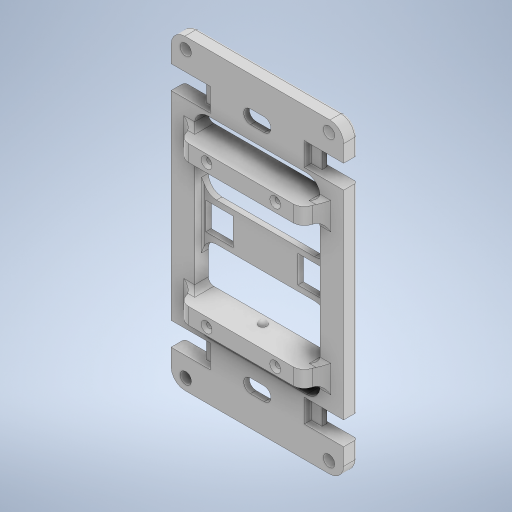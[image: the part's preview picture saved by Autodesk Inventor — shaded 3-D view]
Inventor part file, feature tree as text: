
AUTODESK INVENTOR PART (.ipt)
format: ipt  version: 2023 (Build 270158000, 158)  size: 604,672 bytes
history: native  units: mm
features: extrude x11, sketch x10, fillet x9, other x3, mirror x3, chamfer x1, revolve x1, projected_geometry x1
ambient origin geometry x8: Origin, YZ Plane, XZ Plane, XY Plane, X Axis, Y Axis, Z Axis, Center Point
bodies: Body1 (feature_tree)
feature tree (39):
  other  "솔리드1"
  extrude  "돌출1"  Depth=63.1mm
  extrude  "돌출2"  Depth=112.2mm
  extrude  "돌출3"  Depth=45.85mm
  fillet  "모깎기1"  Radius=70.23mm
  sketch  "스케치4"
  extrude  "돌출4"  Depth=5.0mm TaperAngle=0.0deg
  extrude  "돌출5"  Depth=5.0mm
  mirror  "미러1"
  mirror  "미러2"
  extrude  "돌출6"  Depth=5.0mm
  fillet  "모깎기2"  Radius=5.0mm
  mirror  "미러3"
  fillet  "모깎기3"  Radius=10.0mm
  extrude  "돌출7"  Depth=104.0mm
  fillet  "모깎기4"  Radius=4.2mm
  fillet  "모깎기5"  Radius=52.4mm
  other  "작업 평면1"
  sketch  "스케치9"
  extrude  "돌출8"  TaperAngle=0.0deg  [1 undecoded]
  extrude  "돌출9"  Depth=5.0mm
  fillet  "모깎기7"  Radius=7.0mm
  fillet  "모깎기8"  Radius=8.5mm
  chamfer  "모따기1"  Distance=3.4mm
  other  "작업 평면2"
  revolve  "회전1"
  extrude  "돌출10"  Depth=11.2mm
  fillet  "모깎기9"  Radius=4.0mm
  fillet  "모깎기10"  [1 undecoded]
  extrude  "돌출11"  Depth=2.5mm TaperAngle=0.0deg
  sketch  "스케치1"
  sketch  "스케치2"
  sketch  "스케치3"
  sketch  "스케치6"
  projected_geometry  "투영된 루프1"
  sketch  "스케치8"
  sketch  "스케치11"
  sketch  "스케치13"
  sketch  "스케치14"
note: 2 required parameter values undecoded (feature->parameter linkage not recoverable at this tier; creation-order binding heuristic only, values carry confidence <= 0.55)
